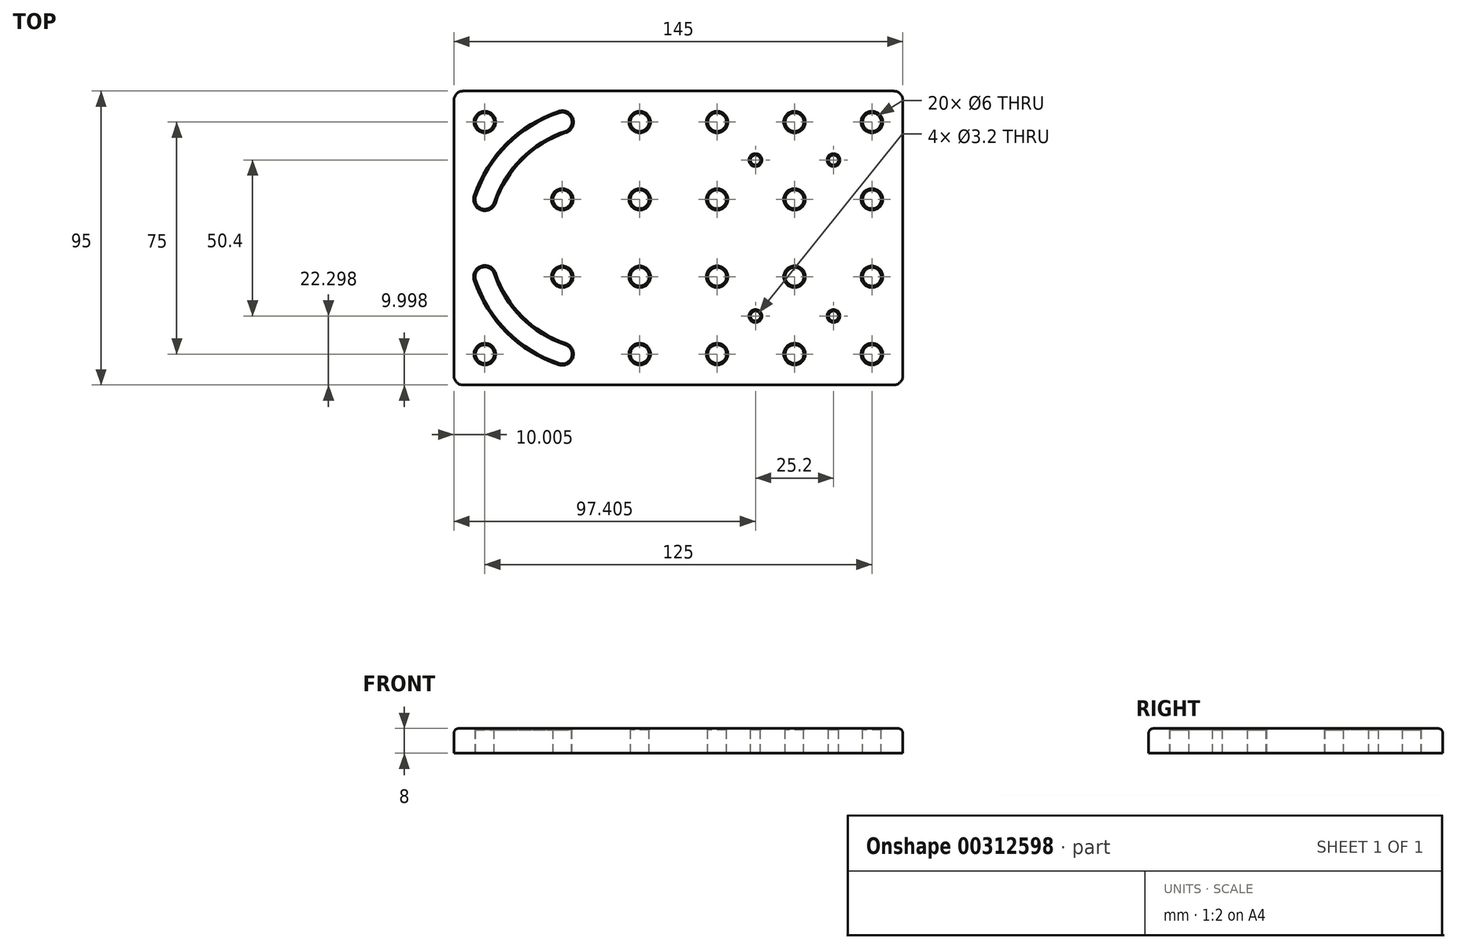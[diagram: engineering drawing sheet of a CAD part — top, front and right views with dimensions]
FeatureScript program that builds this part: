
annotation { "Feature Type Name" : "Feature", "Feature Type Description" : "" }
export const myFeature = defineFeature(function(context is Context, id is Id, definition is map)
    precondition{}
    {
        {
            var Q0;
            Q0=qCreatedBy(makeId("Top.planeOp"),FACE);
            var sketch = newSketch(context, id + "F0", { "sketchPlane" : qUnion([Q0])});
            skCircle(sketch, "E0", {"center": v(5.33, 15.14) * mm, "radius": 1.6 * mm});
            skLineSegment(sketch, "E1.bottom", {"start": v(-117.27, 37.44) * mm, "end": v(27.73, 37.44) * mm});
            skLineSegment(sketch, "E1.top", {"start": v(-117.27, -57.56) * mm, "end": v(27.73, -57.56) * mm});
            skLineSegment(sketch, "E1.left", {"start": v(-117.27, 37.44) * mm, "end": v(-117.27, -57.56) * mm});
            skLineSegment(sketch, "E1.right", {"start": v(27.73, 37.44) * mm, "end": v(27.73, -57.56) * mm});
            skLineSegment(sketch, "E2", {"start": v(-117.27, -10.06) * mm, "end": v(27.73, -10.06) * mm, "construction": true});
            skLineSegment(sketch, "E3", {"start": v(-44.77, 37.44) * mm, "end": v(-44.77, -57.56) * mm, "construction": true});
            skCircle(sketch, "E4.1.0.0", {"center": v(-19.87, 15.14) * mm, "radius": 1.6 * mm});
            skLineSegment(sketch, "E4.direction1", {"start": v(5.33, 15.14) * mm, "end": v(-19.87, 15.14) * mm, "construction": true});
            skCircle(sketch, "E5.MirrorC", {"center": v(-19.87, -35.26) * mm, "radius": 1.6 * mm});
            skCircle(sketch, "E6.MirrorC", {"center": v(5.33, -35.26) * mm, "radius": 1.6 * mm});
            skCircle(sketch, "E7.3.0.0", {"center": v(17.73, 27.44) * mm, "radius": 3 * mm});
            skCircle(sketch, "E8.0.1.0", {"center": v(17.73, 2.44) * mm, "radius": 3 * mm});
            skCircle(sketch, "E8.0.2.0", {"center": v(17.73, -22.56) * mm, "radius": 3 * mm});
            skCircle(sketch, "E8.0.3.0", {"center": v(17.73, -47.56) * mm, "radius": 3 * mm});
            skCircle(sketch, "E8.1.0.0", {"center": v(-7.27, 27.44) * mm, "radius": 3 * mm});
            skCircle(sketch, "E8.1.1.0", {"center": v(-7.27, 2.44) * mm, "radius": 3 * mm});
            skCircle(sketch, "E8.1.2.0", {"center": v(-7.27, -22.56) * mm, "radius": 3 * mm});
            skCircle(sketch, "E8.1.3.0", {"center": v(-7.27, -47.56) * mm, "radius": 3 * mm});
            skCircle(sketch, "E8.2.0.0", {"center": v(-32.27, 27.44) * mm, "radius": 3 * mm});
            skCircle(sketch, "E8.2.1.0", {"center": v(-32.27, 2.44) * mm, "radius": 3 * mm});
            skCircle(sketch, "E8.2.2.0", {"center": v(-32.27, -22.56) * mm, "radius": 3 * mm});
            skCircle(sketch, "E8.2.3.0", {"center": v(-32.27, -47.56) * mm, "radius": 3 * mm});
            skCircle(sketch, "E8.3.0.0", {"center": v(-57.27, 27.44) * mm, "radius": 3 * mm});
            skCircle(sketch, "E8.3.1.0", {"center": v(-57.27, 2.44) * mm, "radius": 3 * mm});
            skCircle(sketch, "E8.3.2.0", {"center": v(-57.27, -22.56) * mm, "radius": 3 * mm});
            skCircle(sketch, "E8.3.3.0", {"center": v(-57.27, -47.56) * mm, "radius": 3 * mm});
            skCircle(sketch, "E8.4.1.0", {"center": v(-82.27, 2.44) * mm, "radius": 3 * mm});
            skCircle(sketch, "E8.4.2.0", {"center": v(-82.27, -22.56) * mm, "radius": 3 * mm});
            skCircle(sketch, "E8.5.0.0", {"center": v(-107.27, 27.44) * mm, "radius": 3 * mm});
            skCircle(sketch, "E8.5.3.0", {"center": v(-107.27, -47.56) * mm, "radius": 3 * mm});
            skLineSegment(sketch, "E8.direction1", {"start": v(17.73, 27.44) * mm, "end": v(-7.27, 27.44) * mm, "construction": true});
            skLineSegment(sketch, "E8.direction2", {"start": v(17.73, 27.44) * mm, "end": v(17.73, 2.44) * mm, "construction": true});
            skLineSegment(sketch, "E9", {"start": v(-57.27, -22.56) * mm, "end": v(-82.27, 2.44) * mm, "construction": true});
            skLineSegment(sketch, "E10", {"start": v(-57.27, 2.44) * mm, "end": v(-82.27, -22.56) * mm, "construction": true});
            skPoint(sketch, "E11", {"position": v(-69.77, -10.06) * mm});
            skArc(sketch, "E12.trimOffspring", {"start": v(-79.24, 28.31) * mm, "mid": v(-97.72, 17.89) * mm, "end": v(-108.14, -0.59) * mm, "construction": true});
            skArc(sketch, "E13.0", {"start": v(-83.26, 30.43) * mm, "mid": v(-99.94, 20.12) * mm, "end": v(-110.25, 3.43) * mm});
            skArc(sketch, "E14.0", {"start": v(-81.27, 24.45) * mm, "mid": v(-95.49, 15.66) * mm, "end": v(-104.28, 1.44) * mm});
            skArc(sketch, "E15.MirrorCS", {"start": v(-110.25, -23.56) * mm, "mid": v(-108.26, -19.57) * mm, "end": v(-104.28, -21.57) * mm});
            skArc(sketch, "E16.MirrorCS", {"start": v(-81.27, -44.57) * mm, "mid": v(-95.49, -35.79) * mm, "end": v(-104.28, -21.57) * mm});
            skArc(sketch, "E17.MirrorCS", {"start": v(-81.27, -44.57) * mm, "mid": v(-79.28, -48.56) * mm, "end": v(-83.26, -50.55) * mm});
            skArc(sketch, "E18.MirrorCS", {"start": v(-83.26, -50.55) * mm, "mid": v(-99.94, -40.24) * mm, "end": v(-110.25, -23.56) * mm});
            skArc(sketch, "E19", {"start": v(-81.27, 24.45) * mm, "mid": v(-79.28, 28.43) * mm, "end": v(-83.26, 30.43) * mm});
            skArc(sketch, "E20", {"start": v(-110.25, 3.43) * mm, "mid": v(-108.26, -0.55) * mm, "end": v(-104.28, 1.44) * mm});
            skSolve(sketch);
        }
        {
            var Q0;
            Q0=makeQuery(id+"F0.imprint","IMPRINT",FACE,{"disambiguationData":[TD([[makeQuery(id+"F0.imprint","IMPRINT",EDGE,{"derivedFrom":sQuery(id+"F0.wireOp",EDGE,"E1.bottom")}),-1.0]])]});
            extrude(context, id + "F1", {"entities" : qUnion([Q0]), "oppositeDirection" : true, "depth" : 8 * mm});
        }
        {
            var Q0;
            Q0=makeQuery(id+"F1.opExtrude","CAP_EDGE",EDGE,{"disambiguationData":[OSD([sQuery(id+"F0.wireOp",EDGE,"j3KSbdT7-v52l-zCZt-XGRu-A8qvlXynsV6m.left")])],"isStart":true});
            var Q1;
            Q1=makeQuery(id+"F1.opExtrude","CAP_EDGE",EDGE,{"disambiguationData":[OSD([sQuery(id+"F0.wireOp",EDGE,"j3KSbdT7-v52l-zCZt-XGRu-A8qvlXynsV6m.top")])],"isStart":true});
            var Q2;
            Q2=makeQuery(id+"F1.opExtrude","CAP_EDGE",EDGE,{"disambiguationData":[OSD([sQuery(id+"F0.wireOp",EDGE,"j3KSbdT7-v52l-zCZt-XGRu-A8qvlXynsV6m.bottom")])],"isStart":true});
            var Q3;
            Q3=makeQuery(id+"F1.opExtrude","CAP_EDGE",EDGE,{"disambiguationData":[OSD([sQuery(id+"F0.wireOp",EDGE,"j3KSbdT7-v52l-zCZt-XGRu-A8qvlXynsV6m.right")])],"isStart":true});
            var Q4;
            Q4=makeQuery(id+"F1.opExtrude","CAP_EDGE",EDGE,{"disambiguationData":[OSD([sQuery(id+"F0.wireOp",EDGE,"E1.left")])],"isStart":true});
            var Q5;
            Q5=makeQuery(id+"F1.opExtrude","CAP_EDGE",EDGE,{"disambiguationData":[OSD([sQuery(id+"F0.wireOp",EDGE,"E1.bottom")])],"isStart":true});
            var Q6;
            Q6=makeQuery(id+"F1.opExtrude","CAP_EDGE",EDGE,{"disambiguationData":[OSD([sQuery(id+"F0.wireOp",EDGE,"E1.top")])],"isStart":true});
            var Q7;
            Q7=makeQuery(id+"F1.opExtrude","CAP_EDGE",EDGE,{"disambiguationData":[OSD([sQuery(id+"F0.wireOp",EDGE,"E1.right")])],"isStart":true});
            fillet(context, id + "F2", {"entities" : qUnion([Q0, Q1, Q2, Q3, Q4, Q5, Q6, Q7]), "radius" : 1.5 * mm, "allowEdgeOverflow" : false});
        }
        {
            var Q0;
            Q0=makeQuery(id+"F1.opExtrude","CAP_EDGE",EDGE,{"disambiguationData":[OSD([sQuery(id+"F0.wireOp",EDGE,"3zgkDINr-Cu18-vCFP-Bt1u-jlhRyPLhL6RZ")])],"isStart":true});
            var Q1;
            Q1=makeQuery(id+"F1.opExtrude","CAP_EDGE",EDGE,{"disambiguationData":[OSD([sQuery(id+"F0.wireOp",EDGE,"E7.1.0.0")])],"isStart":true});
            var Q2;
            Q2=makeQuery(id+"F1.opExtrude","CAP_EDGE",EDGE,{"disambiguationData":[OSD([sQuery(id+"F0.wireOp",EDGE,"E7.1.1.0")])],"isStart":true});
            var Q3;
            Q3=makeQuery(id+"F1.opExtrude","CAP_EDGE",EDGE,{"disambiguationData":[OSD([sQuery(id+"F0.wireOp",EDGE,"7dbd3e61-ddc7-4fd2-b979-d2e7bbc7fccb.2.0.0")])],"isStart":true});
            var Q4;
            Q4=makeQuery(id+"F1.opExtrude","CAP_EDGE",EDGE,{"disambiguationData":[OSD([sQuery(id+"F0.wireOp",EDGE,"7dbd3e61-ddc7-4fd2-b979-d2e7bbc7fccb.2.3.0")])],"isStart":true});
            var Q5;
            Q5=makeQuery(id+"F1.opExtrude","CAP_EDGE",EDGE,{"disambiguationData":[OSD([sQuery(id+"F0.wireOp",EDGE,"7dbd3e61-ddc7-4fd2-b979-d2e7bbc7fccb.1.2.0")])],"isStart":true});
            var Q6;
            Q6=makeQuery(id+"F1.opExtrude","CAP_EDGE",EDGE,{"disambiguationData":[OSD([sQuery(id+"F0.wireOp",EDGE,"7dbd3e61-ddc7-4fd2-b979-d2e7bbc7fccb.1.1.0")])],"isStart":true});
            var Q7;
            Q7=makeQuery(id+"F1.opExtrude","CAP_EDGE",EDGE,{"disambiguationData":[OSD([sQuery(id+"F0.wireOp",EDGE,"7dbd3e61-ddc7-4fd2-b979-d2e7bbc7fccb.0.1.0")])],"isStart":true});
            var Q8;
            Q8=makeQuery(id+"F1.opExtrude","CAP_FACE",FACE,{"disambiguationData":[OSD([sQuery(id+"F0.wireOp",EDGE,"MePs7pbw-vReU-vrTN-x30P-UBN7t9paAV1h"),sQuery(id+"F0.wireOp",EDGE,"ab844eae-ecb3-4c94-bb7f-ad267a5bbaad.0"),sQuery(id+"F0.wireOp",EDGE,"69f91fc3-5977-44d0-8c16-b4abb8640dd5"),sQuery(id+"F0.wireOp",EDGE,"0b46f9c5-eefe-4ec6-b567-0adab7527bec"),sQuery(id+"F0.wireOp",EDGE,"3zgkDINr-Cu18-vCFP-Bt1u-jlhRyPLhL6RZ"),sQuery(id+"F0.wireOp",EDGE,"E1.bottom"),sQuery(id+"F0.wireOp",EDGE,"E1.top"),sQuery(id+"F0.wireOp",EDGE,"E1.left"),sQuery(id+"F0.wireOp",EDGE,"E1.right"),sQuery(id+"F0.wireOp",EDGE,"12a7fad6-629b-4339-aab3-dbb3c9477b270.MirrorCS"),sQuery(id+"F0.wireOp",EDGE,"12a7fad6-629b-4339-aab3-dbb3c9477b271.MirrorCS"),sQuery(id+"F0.wireOp",EDGE,"12a7fad6-629b-4339-aab3-dbb3c9477b274.MirrorCS"),sQuery(id+"F0.wireOp",EDGE,"12a7fad6-629b-4339-aab3-dbb3c9477b275.MirrorCS"),sQuery(id+"F0.wireOp",EDGE,"E4.1.0.0"),sQuery(id+"F0.wireOp",EDGE,"E0"),sQuery(id+"F0.wireOp",EDGE,"E5.MirrorC"),sQuery(id+"F0.wireOp",EDGE,"E6.MirrorC"),sQuery(id+"F0.wireOp",EDGE,"E7.1.0.0"),sQuery(id+"F0.wireOp",EDGE,"E7.1.1.0"),sQuery(id+"F0.wireOp",EDGE,"E7.1.2.0"),sQuery(id+"F0.wireOp",EDGE,"E7.1.3.0"),sQuery(id+"F0.wireOp",EDGE,"E7.2.0.0"),sQuery(id+"F0.wireOp",EDGE,"E7.2.1.0"),sQuery(id+"F0.wireOp",EDGE,"E7.2.2.0"),sQuery(id+"F0.wireOp",EDGE,"E7.2.3.0"),sQuery(id+"F0.wireOp",EDGE,"E7.3.0.0"),sQuery(id+"F0.wireOp",EDGE,"E7.3.1.0"),sQuery(id+"F0.wireOp",EDGE,"E7.3.2.0"),sQuery(id+"F0.wireOp",EDGE,"E7.3.3.0"),sQuery(id+"F0.wireOp",EDGE,"7dbd3e61-ddc7-4fd2-b979-d2e7bbc7fccb.0.1.0"),sQuery(id+"F0.wireOp",EDGE,"7dbd3e61-ddc7-4fd2-b979-d2e7bbc7fccb.0.2.0"),sQuery(id+"F0.wireOp",EDGE,"7dbd3e61-ddc7-4fd2-b979-d2e7bbc7fccb.0.3.0"),sQuery(id+"F0.wireOp",EDGE,"7dbd3e61-ddc7-4fd2-b979-d2e7bbc7fccb.1.1.0"),sQuery(id+"F0.wireOp",EDGE,"7dbd3e61-ddc7-4fd2-b979-d2e7bbc7fccb.1.2.0"),sQuery(id+"F0.wireOp",EDGE,"7dbd3e61-ddc7-4fd2-b979-d2e7bbc7fccb.2.0.0"),sQuery(id+"F0.wireOp",EDGE,"7dbd3e61-ddc7-4fd2-b979-d2e7bbc7fccb.2.3.0")])],"isStart":true});
            chamfer(context, id + "F3", {"entities" : qUnion([Q0, Q1, Q2, Q3, Q4, Q5, Q6, Q7, Q8]), "width" : .5 * mm, "tangentPropagation" : true});
        }
        {
            var Q0;
            Q0=makeQuery(id+"F1.opExtrude","SWEPT_EDGE",EDGE,{"disambiguationData":[OSD([sQuery(id+"F0.wireOp",EDGE,"E1.top"),sQuery(id+"F0.wireOp",EDGE,"E1.left")])]});
            var Q1;
            Q1=makeQuery(id+"F1.opExtrude","SWEPT_EDGE",EDGE,{"disambiguationData":[OSD([sQuery(id+"F0.wireOp",EDGE,"E1.top"),sQuery(id+"F0.wireOp",EDGE,"E1.right")])]});
            var Q2;
            Q2=makeQuery(id+"F1.opExtrude","SWEPT_EDGE",EDGE,{"disambiguationData":[OSD([sQuery(id+"F0.wireOp",EDGE,"E1.bottom"),sQuery(id+"F0.wireOp",EDGE,"E1.right")])]});
            var Q3;
            Q3=makeQuery(id+"F1.opExtrude","SWEPT_EDGE",EDGE,{"disambiguationData":[OSD([sQuery(id+"F0.wireOp",EDGE,"E1.bottom"),sQuery(id+"F0.wireOp",EDGE,"E1.left")])]});
            fillet(context, id + "F4", {"entities" : qUnion([Q0, Q1, Q2, Q3]), "radius" : 3 * mm, "tangentPropagation" : true, "allowEdgeOverflow" : false});
        }
    });
